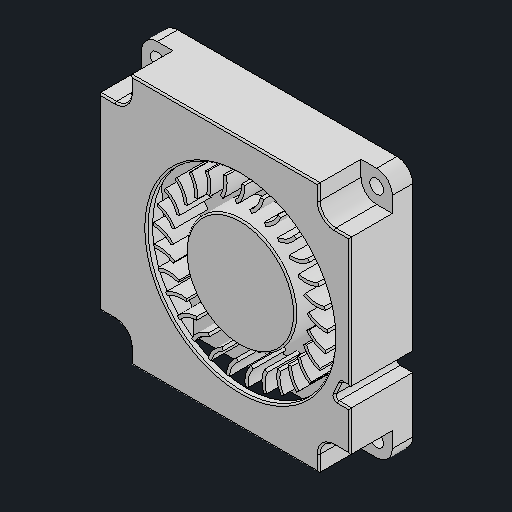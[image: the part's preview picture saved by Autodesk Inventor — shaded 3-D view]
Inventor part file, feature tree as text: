
AUTODESK INVENTOR PART (.ipt)
format: ipt  version: 2024.2 (Build 282272000, 272)  size: 356,864 bytes
history: native  units: mm
features: other x1, fillet x1
ambient origin geometry x8: Origin, YZ Plane, XZ Plane, XY Plane, X Axis, Y Axis, Z Axis, Center Point
bodies: Body1 (feature_tree)
feature tree (2):
  other  "솔리드1"
  fillet  "Fillet2"  [1 undecoded]
note: 1 required parameter value undecoded (feature->parameter linkage not recoverable at this tier; creation-order binding heuristic only, values carry confidence <= 0.55)
